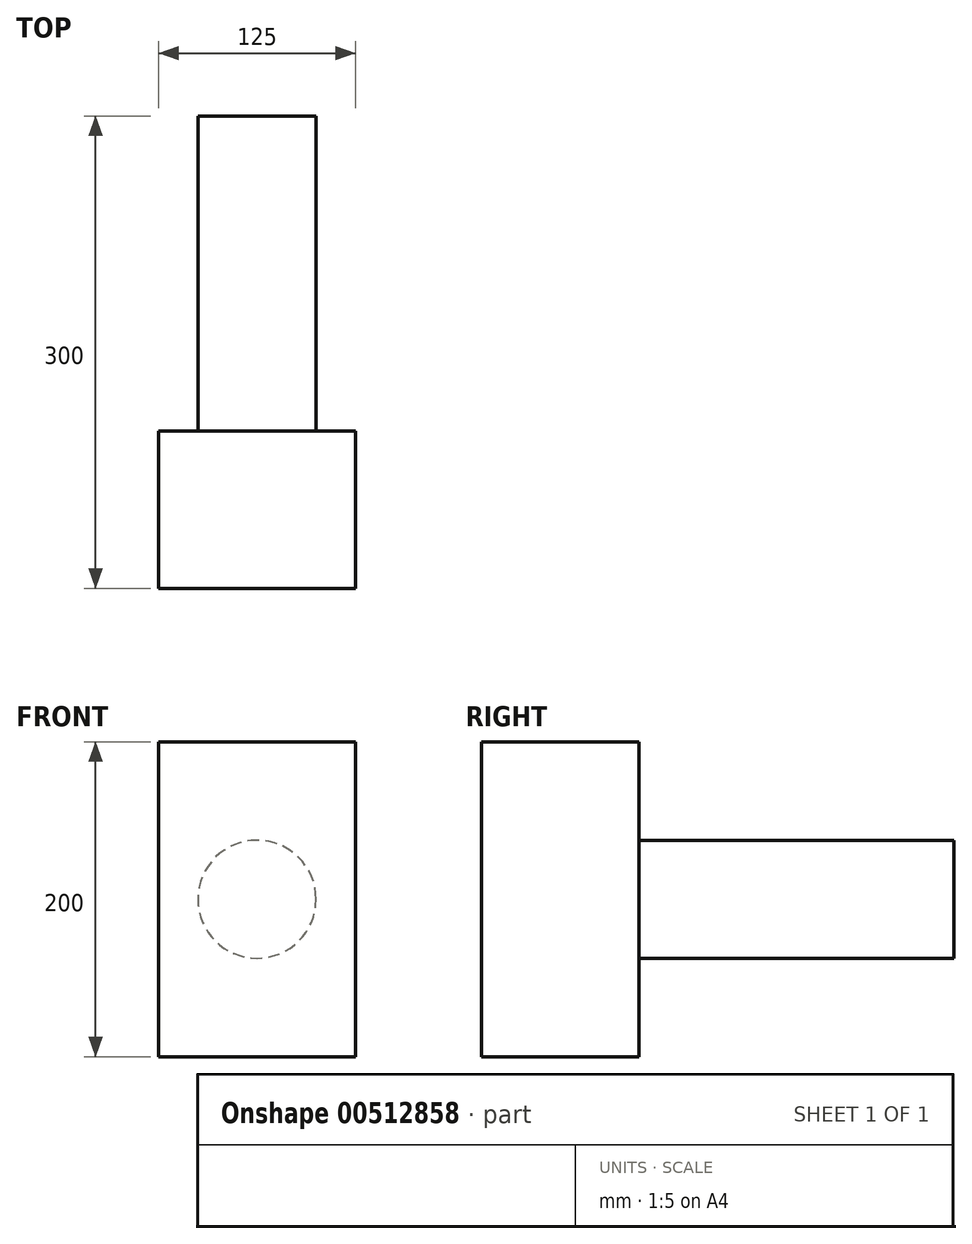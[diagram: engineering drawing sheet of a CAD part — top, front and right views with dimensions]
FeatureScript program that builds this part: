
annotation { "Feature Type Name" : "Feature", "Feature Type Description" : "" }
export const myFeature = defineFeature(function(context is Context, id is Id, definition is map)
    precondition{}
    {
        {
            var Q0;
            Q0=qCreatedBy(makeId("Front.planeOp"),FACE);
            var sketch = newSketch(context, id + "F0", { "sketchPlane" : qUnion([Q0])});
            skCircle(sketch, "E0", {"center": v(0, 0) * mm, "radius": 37.5 * mm});
            skSolve(sketch);
        }
        {
            var Q0;
            Q0 = qSketchRegion(id + "F0", true);
            extrude(context, id + "F1", {"entities" : qUnion([Q0]), "depth" : 200 * mm});
        }
        {
            var Q0;
            Q0=makeQuery(id+"F1.opExtrude","CAP_FACE",FACE,{"disambiguationData":[OSD([sQuery(id+"F0.wireOp",EDGE,"E0")])],"isStart":false});
            var sketch = newSketch(context, id + "F2", { "sketchPlane" : qUnion([Q0])});
            skLineSegment(sketch, "E1.bottom", {"start": v(62.5, 100) * mm, "end": v(-62.5, 100) * mm});
            skLineSegment(sketch, "E1.top", {"start": v(62.5, -100) * mm, "end": v(-62.5, -100) * mm});
            skLineSegment(sketch, "E1.left", {"start": v(62.5, 100) * mm, "end": v(62.5, -100) * mm});
            skLineSegment(sketch, "E1.right", {"start": v(-62.5, 100) * mm, "end": v(-62.5, -100) * mm});
            skPoint(sketch, "E1.middle", {"position": v(0, 0) * mm});
            skSolve(sketch);
        }
        {
            var Q0;
            Q0 = qSketchRegion(id + "F2", true);
            extrude(context, id + "F3", {"entities" : qUnion([Q0]), "operationType" : NewBodyOperationType.ADD, "depth" : 100 * mm});
        }
    });
